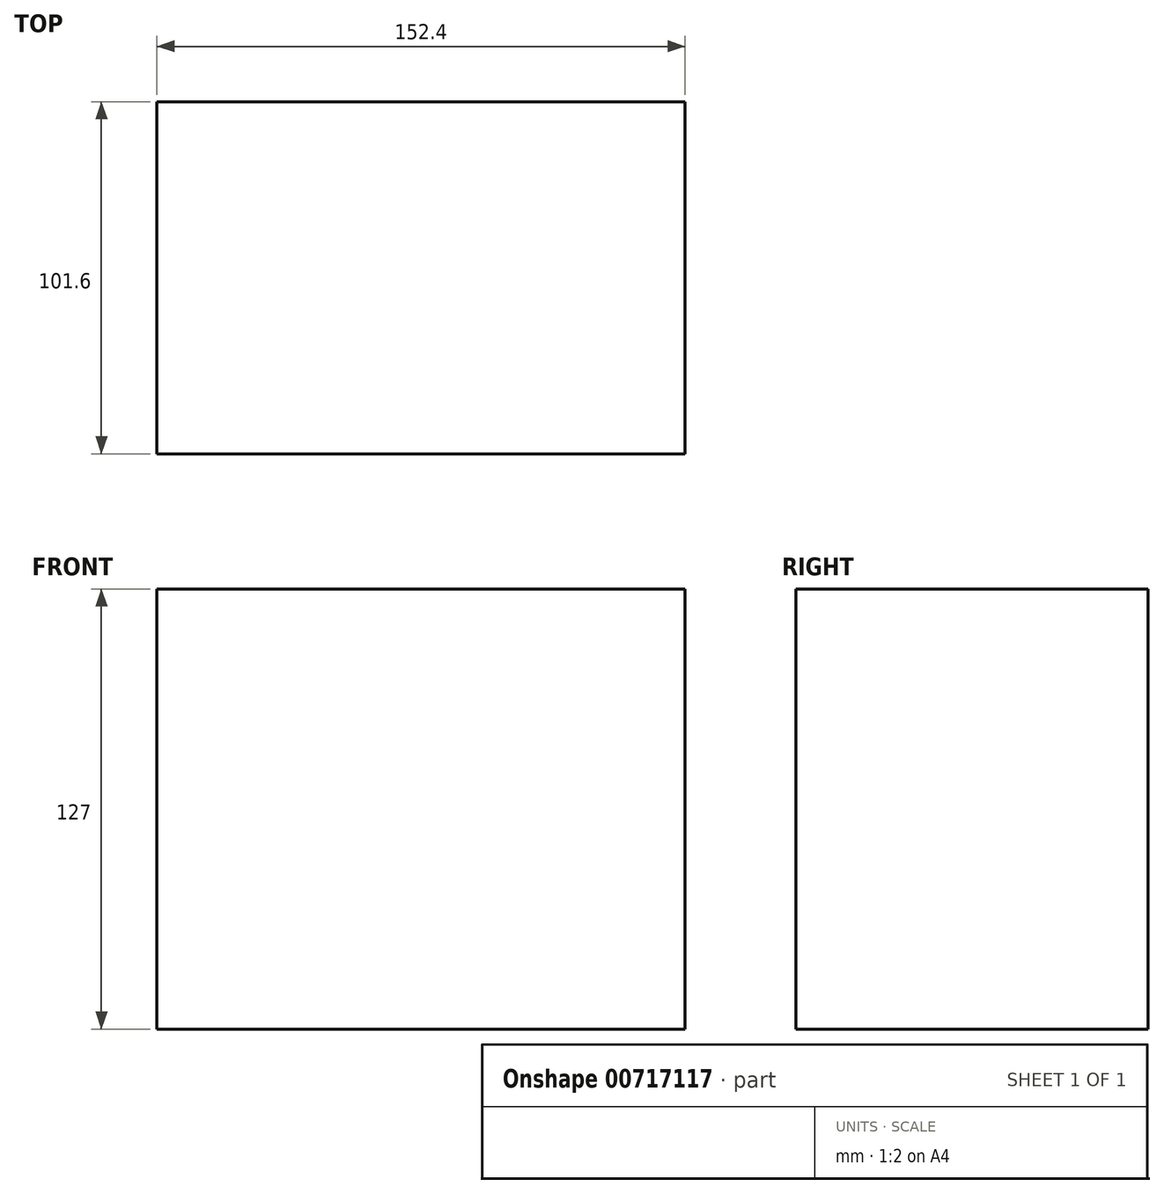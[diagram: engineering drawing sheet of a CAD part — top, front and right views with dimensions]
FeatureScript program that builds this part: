
annotation { "Feature Type Name" : "Feature", "Feature Type Description" : "" }
export const myFeature = defineFeature(function(context is Context, id is Id, definition is map)
    precondition{}
    {
        {
            var Q0;
            Q0=qCreatedBy(makeId("Front.planeOp"),FACE);
            var sketch = newSketch(context, id + "F0", { "sketchPlane" : qUnion([Q0])});
            skLineSegment(sketch, "E0", {"start": v(-73.16, -18.04) * mm, "end": v(79.24, -18.04) * mm});
            skLineSegment(sketch, "E1", {"start": v(79.24, -18.04) * mm, "end": v(79.24, 108.96) * mm});
            skLineSegment(sketch, "E2", {"start": v(79.24, 108.96) * mm, "end": v(-73.16, 108.96) * mm});
            skLineSegment(sketch, "E3", {"start": v(-73.16, 108.96) * mm, "end": v(-73.16, -18.04) * mm});
            skSolve(sketch);
        }
        {
            var Q0;
            Q0=makeQuery(id+"F0.imprint","IMPRINT",FACE,{"disambiguationData":[TD([[makeQuery(id+"F0.imprint","IMPRINT",EDGE,{"derivedFrom":sQuery(id+"F0.wireOp",EDGE,"E0")}),1.0]])]});
            extrude(context, id + "F1", {"entities" : qUnion([Q0]), "depth" : 101.6 * mm, "offsetDistance" : 25.4 * mm});
        }
    });
